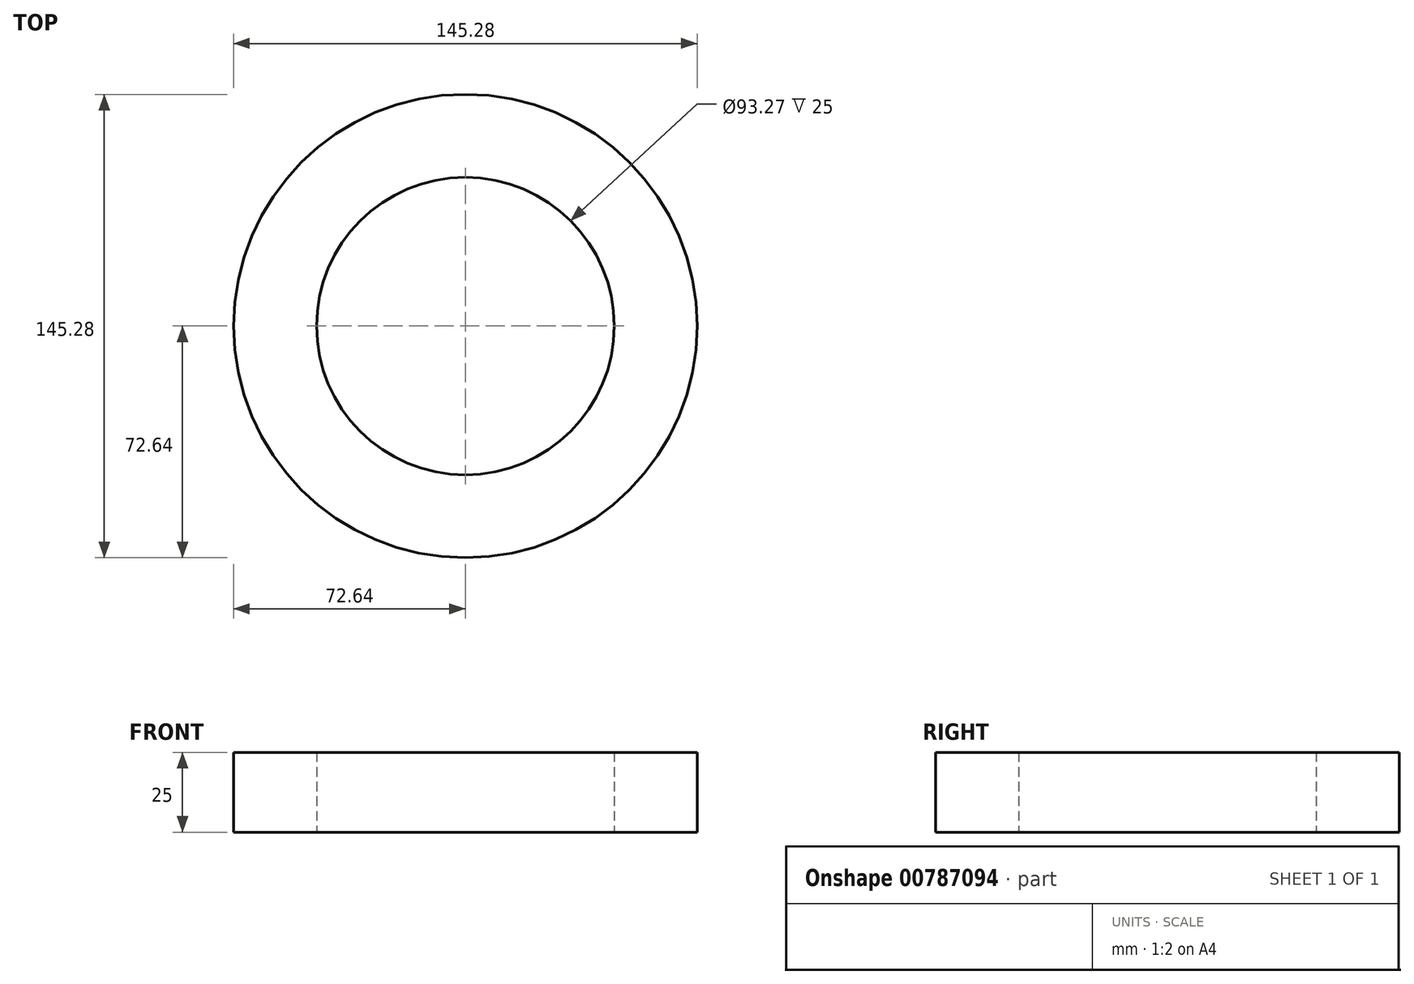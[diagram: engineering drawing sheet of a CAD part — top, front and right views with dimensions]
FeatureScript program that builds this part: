
annotation { "Feature Type Name" : "Feature", "Feature Type Description" : "" }
export const myFeature = defineFeature(function(context is Context, id is Id, definition is map)
    precondition{}
    {
        {
            var Q0;
            Q0=qCreatedBy(makeId("Top.planeOp"),FACE);
            var sketch = newSketch(context, id + "F0", { "sketchPlane" : qUnion([Q0])});
            skCircle(sketch, "E0", {"center": v(0, 0) * mm, "radius": 46.64 * mm});
            skCircle(sketch, "E1.0", {"center": v(0, 0) * mm, "radius": 72.64 * mm});
            skSolve(sketch);
        }
        {
            var Q0;
            Q0 = qSketchRegion(id + "F0", true);
            extrude(context, id + "F1", {"entities" : qUnion([Q0]), "depth" : 25 * mm, "offsetDistance" : 25 * mm});
        }
    });
